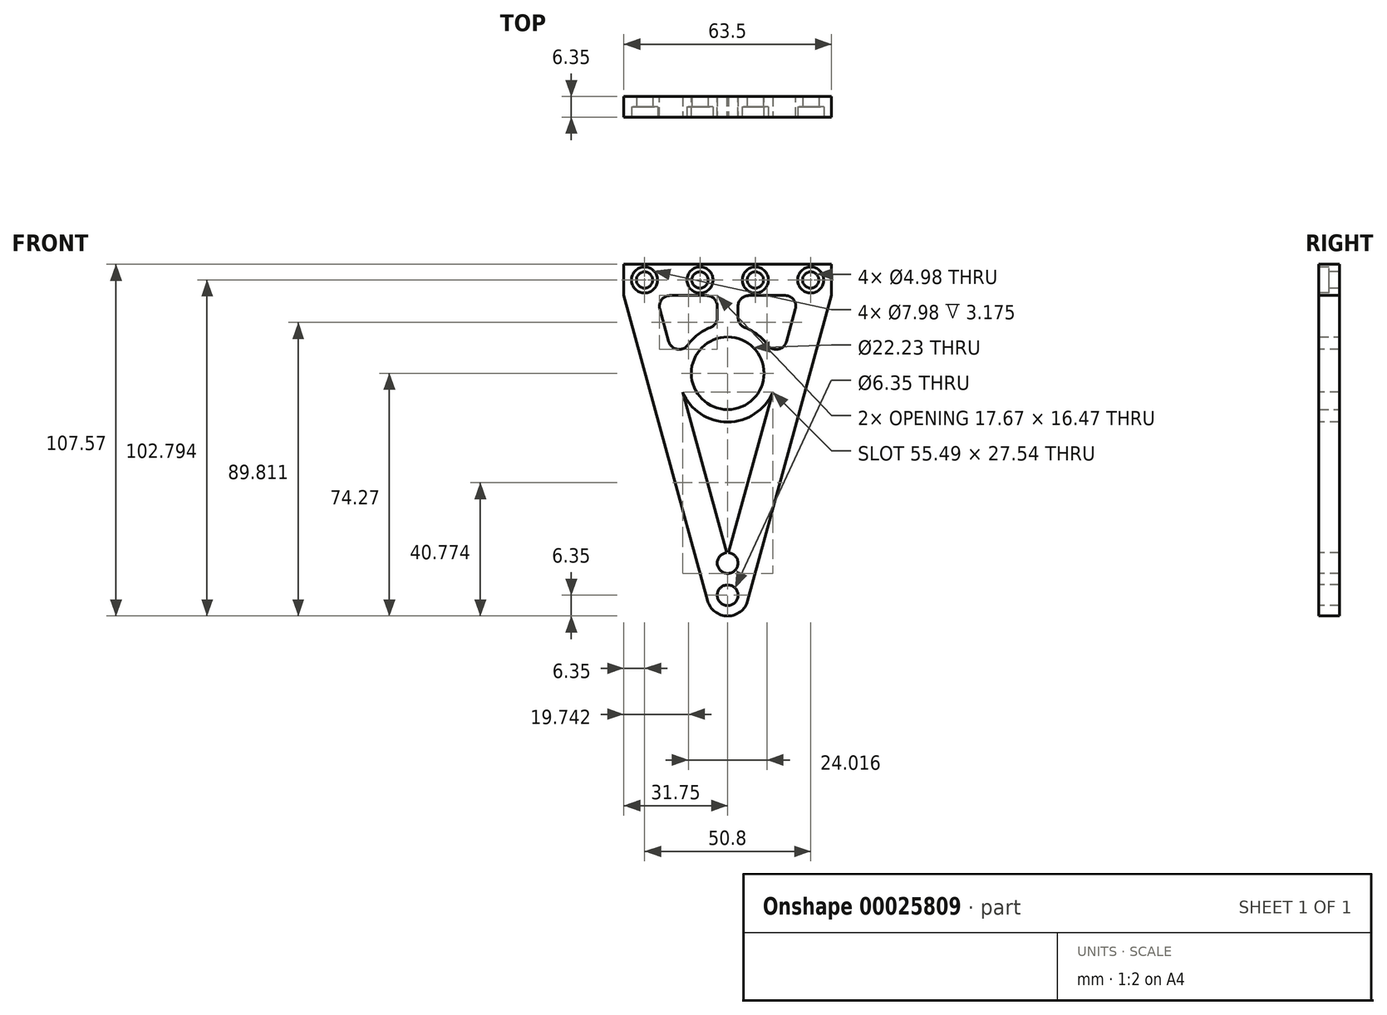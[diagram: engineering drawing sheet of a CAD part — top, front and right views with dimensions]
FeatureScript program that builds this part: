
annotation { "Feature Type Name" : "Feature", "Feature Type Description" : "" }
export const myFeature = defineFeature(function(context is Context, id is Id, definition is map)
    precondition{}
    {
        {
            var Q0;
            Q0=qCreatedBy(makeId("Front.planeOp"),FACE);
            var sketch = newSketch(context, id + "F0", { "sketchPlane" : qUnion([Q0])});
            skCircle(sketch, "E0", {"center": v(0, 0) * mm, "radius": 11.11 * mm});
            skLineSegment(sketch, "E1", {"start": v(0, 49.42) * mm, "end": v(0, 0) * mm, "construction": true});
            skLineSegment(sketch, "E2", {"start": v(47.24, 0) * mm, "end": v(0, 0) * mm, "construction": true});
            skLineSegment(sketch, "E3", {"start": v(-31.75, 33.3) * mm, "end": v(31.75, 33.3) * mm});
            skLineSegment(sketch, "E4", {"start": v(31.75, 33.3) * mm, "end": v(31.75, 23.77) * mm});
            skLineSegment(sketch, "E5", {"start": v(31.75, 23.77) * mm, "end": v(6.12, -69.6) * mm});
            skLineSegment(sketch, "E6", {"start": v(-6.12, -69.6) * mm, "end": v(-31.75, 23.77) * mm});
            skLineSegment(sketch, "E7", {"start": v(-31.75, 23.77) * mm, "end": v(-31.75, 33.3) * mm});
            skArc(sketch, "E8", {"start": v(-6.12, -69.6) * mm, "mid": v(0, -74.27) * mm, "end": v(6.12, -69.6) * mm});
            skPoint(sketch, "E9", {"position": v(0, -74.27) * mm});
            skSolve(sketch);
        }
        {
            var Q0;
            Q0=makeQuery(id+"F0.imprint","IMPRINT",FACE,{"disambiguationData":[TD([[makeQuery(id+"F0.imprint","IMPRINT",EDGE,{"derivedFrom":sQuery(id+"F0.wireOp",EDGE,"E0")}),-1.0]])]});
            var Q1;
            {var subQ5=sQuery(id+"F0.wireOp",EDGE,"E3");Q1=makeQuery(id+"F0.imprint","IMPRINT",FACE,{"disambiguationData":[TD([[makeQuery(id+"F0.imprint","IMPRINT",EDGE,{"derivedFrom":subQ5}),-1.0]])]});}
            extrude(context, id + "F1", {"entities" : qUnion([Q0, Q1]), "depth" : 6.35 * mm});
        }
        {
            var Q0;
            Q0=qCreatedBy(makeId("Front.planeOp"),FACE);
            var sketch = newSketch(context, id + "F2", { "sketchPlane" : qUnion([Q0])});
            skLineSegment(sketch, "E10.0", {"start": v(-21.87, 23.77) * mm, "end": v(-3.17, 23.77) * mm});
            skLineSegment(sketch, "E10.2", {"start": v(0, -55.92) * mm, "end": v(-13.77, -5.75) * mm});
            skLineSegment(sketch, "E10.3", {"start": v(21.87, 23.77) * mm, "end": v(14.78, -2.08) * mm});
            skArc(sketch, "E11", {"start": v(-13.77, -5.75) * mm, "mid": v(0, -14.92) * mm, "end": v(13.77, -5.75) * mm});
            skArc(sketch, "E12.trimOffspring", {"start": v(14.78, -2.08) * mm, "mid": v(12.25, 8.53) * mm, "end": v(3.17, 14.58) * mm});
            skLineSegment(sketch, "E13.trimOffspring", {"start": v(13.77, -5.75) * mm, "end": v(0, -55.92) * mm});
            skLineSegment(sketch, "E14.trimOffspring", {"start": v(-14.78, -2.08) * mm, "end": v(-21.87, 23.77) * mm});
            skLineSegment(sketch, "E15", {"start": v(0, 0) * mm, "end": v(0, 37.9) * mm, "construction": true});
            skCircle(sketch, "E16", {"center": v(0, -49.68) * mm, "radius": 1.65 * mm});
            skLineSegment(sketch, "E17", {"start": v(3.17, 14.58) * mm, "end": v(3.17, 23.77) * mm});
            skLineSegment(sketch, "E18.trimOffspring", {"start": v(3.17, 23.77) * mm, "end": v(21.87, 23.77) * mm});
            skArc(sketch, "E19.trimOffspring", {"start": v(-3.17, 14.58) * mm, "mid": v(-12.25, 8.53) * mm, "end": v(-14.78, -2.08) * mm});
            skLineSegment(sketch, "E20.trimOffspring", {"start": v(-3.17, 23.77) * mm, "end": v(-3.17, 14.58) * mm});
            skSolve(sketch);
        }
        {
            var Q0;
            Q0 = qSketchRegion(id + "F2", true);
            extrude(context, id + "F3", {"entities" : qUnion([Q0]), "operationType" : NewBodyOperationType.ADD, "depth" : 25.4 * mm});
        }
        {
            var Q0;
            Q0=makeQuery(id+"F3.opExtrude","CAP_FACE",FACE,{"disambiguationData":[OSD([sQuery(id+"F2.wireOp",EDGE,"E10.0"),sQuery(id+"F2.wireOp",EDGE,"E14.trimOffspring"),sQuery(id+"F2.wireOp",EDGE,"E19.trimOffspring"),sQuery(id+"F2.wireOp",EDGE,"E20.trimOffspring")])],"isStart":false});
            var Q1;
            Q1=makeQuery(id+"F3.opExtrude","CAP_FACE",FACE,{"disambiguationData":[OSD([sQuery(id+"F2.wireOp",EDGE,"E10.3"),sQuery(id+"F2.wireOp",EDGE,"E12.trimOffspring"),sQuery(id+"F2.wireOp",EDGE,"E17"),sQuery(id+"F2.wireOp",EDGE,"E18.trimOffspring")])],"isStart":false});
            extrude(context, id + "F4", {"entities" : qUnion([Q0, Q1]), "operationType" : NewBodyOperationType.REMOVE, "oppositeDirection" : true, "depth" : 25.4 * mm});
        }
        {
            var Q0;
            Q0=makeQuery(id+"F3.opExtrude","CAP_FACE",FACE,{"disambiguationData":[OSD([sQuery(id+"F2.wireOp",EDGE,"E10.2"),sQuery(id+"F2.wireOp",EDGE,"E11"),sQuery(id+"F2.wireOp",EDGE,"E13.trimOffspring")])],"isStart":false});
            var Q1;
            Q1 = qSketchRegion(id + "F2", true);
            extrude(context, id + "F5", {"entities" : qUnion([Q0, Q1]), "operationType" : NewBodyOperationType.REMOVE, "oppositeDirection" : true, "depth" : 25.4 * mm});
        }
        {
            var Q0;
            Q0=makeQuery(id+"F4.boolean.opBoolean","COPY",EDGE,{"derivedFrom":makeQuery(id+"F4.opExtrude","SWEPT_EDGE",EDGE,{"disambiguationData":[OSD([sQuery(id+"F2.wireOp",EDGE,"E10.0"),sQuery(id+"F2.wireOp",EDGE,"E14.trimOffspring")])]})});
            var Q1;
            Q1=makeQuery(id+"F4.boolean.opBoolean","COPY",EDGE,{"derivedFrom":makeQuery(id+"F4.opExtrude","SWEPT_EDGE",EDGE,{"disambiguationData":[OSD([sQuery(id+"F2.wireOp",EDGE,"E17"),sQuery(id+"F2.wireOp",EDGE,"E18.trimOffspring")])]})});
            var Q2;
            Q2=makeQuery(id+"F4.boolean.opBoolean","COPY",EDGE,{"derivedFrom":makeQuery(id+"F4.opExtrude","SWEPT_EDGE",EDGE,{"disambiguationData":[OSD([sQuery(id+"F2.wireOp",EDGE,"E10.3"),sQuery(id+"F2.wireOp",EDGE,"E18.trimOffspring")])]})});
            var Q3;
            Q3=makeQuery(id+"F4.boolean.opBoolean","COPY",EDGE,{"derivedFrom":makeQuery(id+"F4.opExtrude","SWEPT_EDGE",EDGE,{"disambiguationData":[OSD([sQuery(id+"F2.wireOp",EDGE,"E10.0"),sQuery(id+"F2.wireOp",EDGE,"E20.trimOffspring")])]})});
            var Q4;
            Q4=makeQuery(id+"F4.boolean.opBoolean","COPY",EDGE,{"derivedFrom":makeQuery(id+"F4.opExtrude","SWEPT_EDGE",EDGE,{"disambiguationData":[OSD([sQuery(id+"F2.wireOp",EDGE,"E12.trimOffspring"),sQuery(id+"F2.wireOp",EDGE,"E17")])]})});
            var Q5;
            Q5=makeQuery(id+"F4.boolean.opBoolean","COPY",EDGE,{"derivedFrom":makeQuery(id+"F4.opExtrude","SWEPT_EDGE",EDGE,{"disambiguationData":[OSD([sQuery(id+"F2.wireOp",EDGE,"E19.trimOffspring"),sQuery(id+"F2.wireOp",EDGE,"E20.trimOffspring")])]})});
            var Q6;
            Q6=makeQuery(id+"F4.boolean.opBoolean","COPY",EDGE,{"derivedFrom":makeQuery(id+"F4.opExtrude","SWEPT_EDGE",EDGE,{"disambiguationData":[OSD([sQuery(id+"F2.wireOp",EDGE,"E10.3"),sQuery(id+"F2.wireOp",EDGE,"E12.trimOffspring")])]})});
            var Q7;
            Q7=makeQuery(id+"F4.boolean.opBoolean","COPY",EDGE,{"derivedFrom":makeQuery(id+"F4.opExtrude","SWEPT_EDGE",EDGE,{"disambiguationData":[OSD([sQuery(id+"F2.wireOp",EDGE,"E14.trimOffspring"),sQuery(id+"F2.wireOp",EDGE,"E19.trimOffspring")])]})});
            var Q8;
            {var subQ0=sQuery(id+"F2.wireOp",EDGE,"E11");var subQ1=sQuery(id+"F2.wireOp",EDGE,"E13.trimOffspring");Q8=makeQuery(id+"F5.boolean.opBoolean","TWEAK_EDGE",EDGE,{"derivedFrom":[makeQuery(id+"F5.opExtrude","SWEPT_EDGE",EDGE,{"disambiguationData":[OSD([subQ0,subQ1]),TDD([makeQuery(id+"F2.imprint","INTERSECT",VERTEX,{"derivedFrom":[subQ0,subQ1]})])]}),makeQuery(id+"F5.opExtrude","SWEPT_EDGE",EDGE,{"disambiguationData":[OSD([subQ0,subQ1]),TDD([makeQuery(id+"F3.opExtrude","CAP_VERTEX",VERTEX,{"disambiguationData":[OSD([subQ0,subQ1])],"isStart":false})])]})]});}
            var Q9;
            {var subQ0=sQuery(id+"F2.wireOp",EDGE,"E10.2");var subQ1=sQuery(id+"F2.wireOp",EDGE,"E11");Q9=makeQuery(id+"F5.boolean.opBoolean","TWEAK_EDGE",EDGE,{"derivedFrom":[makeQuery(id+"F5.opExtrude","SWEPT_EDGE",EDGE,{"disambiguationData":[OSD([subQ0,subQ1]),TDD([makeQuery(id+"F2.imprint","INTERSECT",VERTEX,{"derivedFrom":[subQ0,subQ1]})])]}),makeQuery(id+"F5.opExtrude","SWEPT_EDGE",EDGE,{"disambiguationData":[OSD([subQ0,subQ1]),TDD([makeQuery(id+"F3.opExtrude","CAP_VERTEX",VERTEX,{"disambiguationData":[OSD([subQ0,subQ1])],"isStart":false})])]})]});}
            var Q10;
            {var subQ0=sQuery(id+"F2.wireOp",EDGE,"E10.2");var subQ1=sQuery(id+"F2.wireOp",EDGE,"E13.trimOffspring");Q10=makeQuery(id+"F5.boolean.opBoolean","TWEAK_EDGE",EDGE,{"derivedFrom":[makeQuery(id+"F5.opExtrude","SWEPT_EDGE",EDGE,{"disambiguationData":[OSD([subQ0,subQ1]),TDD([makeQuery(id+"F2.imprint","INTERSECT",VERTEX,{"derivedFrom":[subQ0,subQ1]})])]}),makeQuery(id+"F5.opExtrude","SWEPT_EDGE",EDGE,{"disambiguationData":[OSD([subQ0,subQ1]),TDD([makeQuery(id+"F3.opExtrude","CAP_VERTEX",VERTEX,{"disambiguationData":[OSD([subQ0,subQ1])],"isStart":false})])]})]});}
            fillet(context, id + "F6", {"entities" : qUnion([Q0, Q1, Q2, Q3, Q4, Q5, Q6, Q7, Q8, Q9, Q10]), "radius" : 3.3 * mm, "tangentPropagation" : true, "allowEdgeOverflow" : false});
        }
        {
            var Q0;
            Q0=makeQuery(id+"F1.opExtrude","CAP_FACE",FACE,{"disambiguationData":[OSD([sQuery(id+"F0.wireOp",EDGE,"E0"),sQuery(id+"F0.wireOp",EDGE,"E3"),sQuery(id+"F0.wireOp",EDGE,"E4"),sQuery(id+"F0.wireOp",EDGE,"E5"),sQuery(id+"F0.wireOp",EDGE,"E6"),sQuery(id+"F0.wireOp",EDGE,"E7"),sQuery(id+"F0.wireOp",EDGE,"E8")])],"isStart":false});
            var sketch = newSketch(context, id + "F7", { "sketchPlane" : qUnion([Q0])});
            skLineSegment(sketch, "E21", {"start": v(-32.96, 28.52) * mm, "end": v(70.24, 28.52) * mm});
            skPoint(sketch, "E22", {"position": v(-25.4, 28.52) * mm});
            skPoint(sketch, "E23", {"position": v(-8.46, 28.52) * mm});
            skPoint(sketch, "E24", {"position": v(8.46, 28.52) * mm});
            skPoint(sketch, "E25", {"position": v(25.4, 28.52) * mm});
            skSolve(sketch);
        }
        {
            var Q0;
            Q0=sQuery(id+"F7.wireOp",VERTEX,"E22");
            var Q1;
            Q1=sQuery(id+"F7.wireOp",VERTEX,"E23");
            var Q2;
            Q2=sQuery(id+"F7.wireOp",VERTEX,"E24");
            var Q3;
            Q3=sQuery(id+"F7.wireOp",VERTEX,"E25");
            var Q4;
            Q4=makeQuery(id+"F1.opExtrude","SWEPT_BODY",BODY,{"disambiguationData":[OSD([sQuery(id+"F0.wireOp",EDGE,"E0"),sQuery(id+"F0.wireOp",EDGE,"E3"),sQuery(id+"F0.wireOp",EDGE,"E4"),sQuery(id+"F0.wireOp",EDGE,"E5"),sQuery(id+"F0.wireOp",EDGE,"E6"),sQuery(id+"F0.wireOp",EDGE,"E7"),sQuery(id+"F0.wireOp",EDGE,"E8")])]});
            hole(context, id + "F8", {"style" : HoleStyle.C_BORE, "holeDiameter" : 4.98 * mm, "cBoreDiameter" : 7.98 * mm, "cBoreDepth" : 3.17 * mm, "endStyle" : HoleEndStyle.THROUGH, "locations" : qUnion([Q0, Q1, Q2, Q3]), "scope" : qUnion([Q4])});
        }
        {
            var Q0;
            Q0=makeQuery(id+"F1.opExtrude","CAP_FACE",FACE,{"disambiguationData":[OSD([sQuery(id+"F0.wireOp",EDGE,"E0"),sQuery(id+"F0.wireOp",EDGE,"E3"),sQuery(id+"F0.wireOp",EDGE,"E4"),sQuery(id+"F0.wireOp",EDGE,"E5"),sQuery(id+"F0.wireOp",EDGE,"E6"),sQuery(id+"F0.wireOp",EDGE,"E7"),sQuery(id+"F0.wireOp",EDGE,"E8")])],"isStart":false});
            var sketch = newSketch(context, id + "F9", { "sketchPlane" : qUnion([Q0])});
            skLineSegment(sketch, "E26", {"start": v(0, 37.58) * mm, "end": v(0, -79.68) * mm});
            skPoint(sketch, "E27", {"position": v(0, -58.06) * mm});
            skPoint(sketch, "E28", {"position": v(0, -67.92) * mm});
            skSolve(sketch);
        }
        {
            var Q0;
            Q0=sQuery(id+"F9.wireOp",VERTEX,"E27");
            var Q1;
            Q1=sQuery(id+"F9.wireOp",VERTEX,"E28");
            var Q2;
            Q2=makeQuery(id+"F1.opExtrude","SWEPT_BODY",BODY,{"disambiguationData":[OSD([sQuery(id+"F0.wireOp",EDGE,"E0"),sQuery(id+"F0.wireOp",EDGE,"E3"),sQuery(id+"F0.wireOp",EDGE,"E4"),sQuery(id+"F0.wireOp",EDGE,"E5"),sQuery(id+"F0.wireOp",EDGE,"E6"),sQuery(id+"F0.wireOp",EDGE,"E7"),sQuery(id+"F0.wireOp",EDGE,"E8")])]});
            hole(context, id + "F10", {"style" : HoleStyle.SIMPLE, "holeDiameter" : 6.35 * mm, "endStyle" : HoleEndStyle.THROUGH, "locations" : qUnion([Q0, Q1]), "scope" : qUnion([Q2])});
        }
    });
